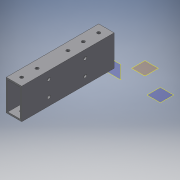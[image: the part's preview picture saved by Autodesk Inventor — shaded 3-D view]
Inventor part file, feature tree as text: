
AUTODESK INVENTOR PART (.ipt)
format: ipt  version: 2018 (Build 220112000, 112)  size: 166,400 bytes
history: native  units: in
note: dims shown in document units (in); Inventor stores cm internally (conversion verified against a paired STEP export)
features: plane x4, extrude x4, sketch x4
ambient origin geometry x8: Origin, YZ Plane, XZ Plane, XY Plane, X Axis, Y Axis, Z Axis, Center Point
bodies: Body1 (feature_tree)
feature tree (12):
  plane  "Work Plane1"
  extrude  "Extrusion16"  TaperAngle=0.0deg  [1 undecoded]
  plane  "Work Plane4"
  extrude  "Extrusion17"  Depth=6.0in
  plane  "Work Plane3"
  extrude  "Extrusion22"  Depth=0.5in
  plane  "Work Plane2"
  extrude  "Extrusion23"  Depth=2.0in
  sketch  "Sketch20"  dims[d71=1.0in d72=2.0in d73=0.1in d74=0.1in d75=0.1in d76=0.1in d77=0.1in d78=0.0in]
  sketch  "Sketch21"  dims[d79=6.0in d80=0.0in d81=0.5in]
  sketch  "Sketch26"  dims[d82=0.5in d83=0.5in]
  sketch  "Sketch27"  dims[d84=1.0in d85=0.5in d86=0.2031in d87=0.2031in d88=0.2031in d89=1.0in d90=1.0in d91=1.0in d92=0.2031in d93=0.2031in d94=0.5in d95=0.5in d96=3.0in d97=0.0in d122=0.2031in d123=1.765in d124=0.491in d125=0.2031in d126=2.355in d129=1.0in d130=0.2031in d131=1.0in d132=0.2031in d133=1.0in d134=0.0in d135=0.5in d136=0.5in d137=1.5in d138=0.5in d139=0.2031in d140=0.2031in d141=2.0in d142=0.0in]
note: 1 required parameter value undecoded (feature->parameter linkage not recoverable at this tier; creation-order binding heuristic only, values carry confidence <= 0.55)
